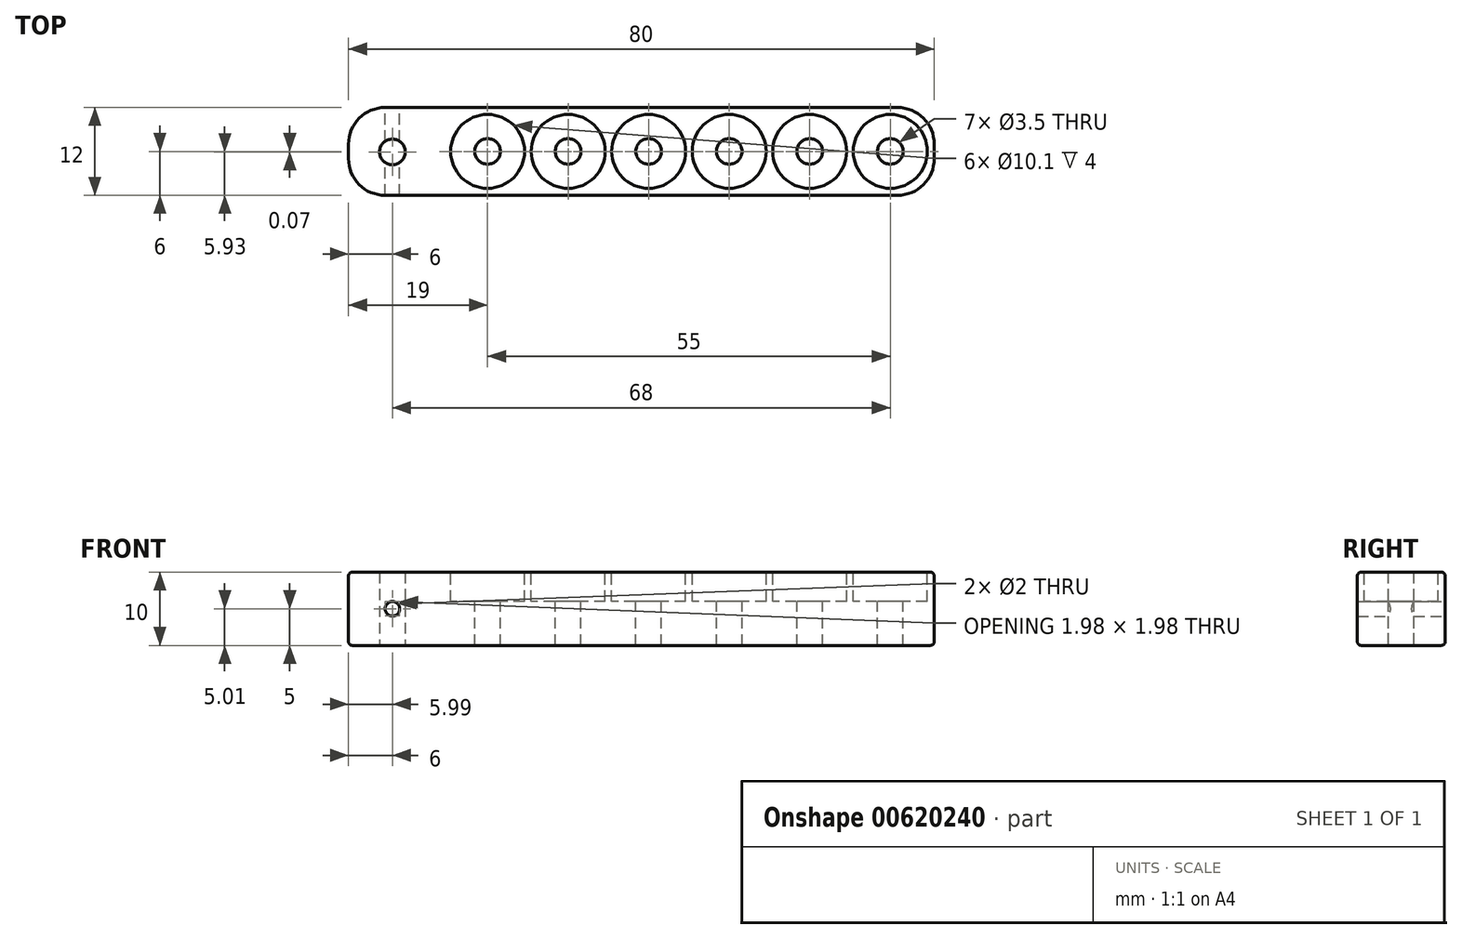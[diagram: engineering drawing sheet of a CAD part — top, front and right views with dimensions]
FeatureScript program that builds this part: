
annotation { "Feature Type Name" : "Feature", "Feature Type Description" : "" }
export const myFeature = defineFeature(function(context is Context, id is Id, definition is map)
    precondition{}
    {
        {
            var Q0;
            Q0=qCreatedBy(makeId("Top.planeOp"),FACE);
            var sketch = newSketch(context, id + "F0", { "sketchPlane" : qUnion([Q0])});
            skLineSegment(sketch, "E0.bottom", {"start": v(40, 6) * mm, "end": v(-40, 6) * mm});
            skLineSegment(sketch, "E0.top", {"start": v(40, -6) * mm, "end": v(-40, -6) * mm});
            skLineSegment(sketch, "E0.left", {"start": v(40, 6) * mm, "end": v(40, -6) * mm});
            skLineSegment(sketch, "E0.right", {"start": v(-40, 6) * mm, "end": v(-40, -6) * mm});
            skPoint(sketch, "E0.middle", {"position": v(0, 0) * mm});
            skSolve(sketch);
        }
        {
            var Q0;
            Q0=makeQuery(id+"F0.imprint","IMPRINT",FACE,{"disambiguationData":[TD([[makeQuery(id+"F0.imprint","IMPRINT",EDGE,{"derivedFrom":sQuery(id+"F0.wireOp",EDGE,"E0.bottom")}),1.0]])]});
            extrude(context, id + "F1", {"entities" : qUnion([Q0]), "depth" : 10 * mm, "offsetDistance" : 25 * mm});
        }
        {
            var Q0;
            Q0=makeQuery(id+"F1.opExtrude","CAP_FACE",FACE,{"disambiguationData":[OSD([sQuery(id+"F0.wireOp",EDGE,"E0.bottom"),sQuery(id+"F0.wireOp",EDGE,"E0.top"),sQuery(id+"F0.wireOp",EDGE,"E0.left"),sQuery(id+"F0.wireOp",EDGE,"E0.right")])],"isStart":false});
            var sketch = newSketch(context, id + "F2", { "sketchPlane" : qUnion([Q0])});
            skLineSegment(sketch, "E1", {"start": v(40, 0) * mm, "end": v(-40, 0) * mm, "construction": true});
            skCircle(sketch, "E2", {"center": v(34, 0) * mm, "radius": 5.05 * mm});
            skCircle(sketch, "E3", {"center": v(23, 0) * mm, "radius": 5.05 * mm});
            skCircle(sketch, "E4", {"center": v(12, 0) * mm, "radius": 5.05 * mm});
            skCircle(sketch, "E5", {"center": v(1, 0) * mm, "radius": 5.05 * mm});
            skCircle(sketch, "E6", {"center": v(-10, 0) * mm, "radius": 5.05 * mm});
            skCircle(sketch, "E7", {"center": v(-21, 0) * mm, "radius": 5.05 * mm});
            skSolve(sketch);
        }
        {
            var Q0;
            Q0 = qSketchRegion(id + "F2", true);
            extrude(context, id + "F3", {"entities" : qUnion([Q0]), "operationType" : NewBodyOperationType.REMOVE, "oppositeDirection" : true, "depth" : 4 * mm, "offsetDistance" : 25 * mm});
        }
        {
            var Q0;
            Q0=makeQuery(id+"F1.opExtrude","SWEPT_EDGE",EDGE,{"disambiguationData":[OSD([sQuery(id+"F0.wireOp",EDGE,"E0.top"),sQuery(id+"F0.wireOp",EDGE,"E0.left")])]});
            fillet(context, id + "F4", {"entities" : qUnion([Q0]), "radius" : 5 * mm, "tangentPropagation" : true, "allowEdgeOverflow" : false});
        }
        {
            var Q0;
            Q0=makeQuery(id+"F1.opExtrude","SWEPT_EDGE",EDGE,{"disambiguationData":[OSD([sQuery(id+"F0.wireOp",EDGE,"E0.bottom"),sQuery(id+"F0.wireOp",EDGE,"E0.left")])]});
            var Q1;
            Q1=makeQuery(id+"F1.opExtrude","SWEPT_EDGE",EDGE,{"disambiguationData":[OSD([sQuery(id+"F0.wireOp",EDGE,"E0.top"),sQuery(id+"F0.wireOp",EDGE,"E0.right")])]});
            var Q2;
            Q2=makeQuery(id+"F1.opExtrude","SWEPT_EDGE",EDGE,{"disambiguationData":[OSD([sQuery(id+"F0.wireOp",EDGE,"E0.bottom"),sQuery(id+"F0.wireOp",EDGE,"E0.right")])]});
            fillet(context, id + "F5", {"entities" : qUnion([Q0, Q1, Q2]), "radius" : 5 * mm, "tangentPropagation" : true, "allowEdgeOverflow" : false});
        }
        {
            var Q0;
            Q0=makeQuery(id+"F3.boolean.opBoolean","COPY",FACE,{"derivedFrom":makeQuery(id+"F3.opExtrude","CAP_FACE",FACE,{"disambiguationData":[OSD([sQuery(id+"F2.wireOp",EDGE,"E7")])],"isStart":false})});
            var sketch = newSketch(context, id + "F6", { "sketchPlane" : qUnion([Q0])});
            skLineSegment(sketch, "E8", {"start": v(-39.92, 0) * mm, "end": v(40.18, 0) * mm, "construction": true});
            skCircle(sketch, "E9", {"center": v(34, 0) * mm, "radius": 1.75 * mm});
            skCircle(sketch, "E10", {"center": v(23, 0) * mm, "radius": 1.75 * mm});
            skCircle(sketch, "E11", {"center": v(12, 0) * mm, "radius": 1.75 * mm});
            skCircle(sketch, "E12", {"center": v(1, 0) * mm, "radius": 1.75 * mm});
            skCircle(sketch, "E13", {"center": v(-10, 0) * mm, "radius": 1.75 * mm});
            skCircle(sketch, "E14", {"center": v(-21, 0) * mm, "radius": 1.75 * mm});
            skSolve(sketch);
        }
        {
            var Q0;
            Q0 = qSketchRegion(id + "F6", true);
            extrude(context, id + "F7", {"entities" : qUnion([Q0]), "operationType" : NewBodyOperationType.REMOVE, "oppositeDirection" : true, "depth" : 25 * mm, "offsetDistance" : 25 * mm});
        }
        {
            var Q0;
            Q0=makeQuery(id+"F1.opExtrude","CAP_EDGE",EDGE,{"disambiguationData":[OSD([sQuery(id+"F0.wireOp",EDGE,"E0.top")])],"isStart":false});
            var Q1;
            {var subQ0=sQuery(id+"F0.wireOp",EDGE,"E0.left");var subQ1=sQuery(id+"F0.wireOp",EDGE,"E0.top");Q1=makeQuery(id+"F4.opFillet","BLEND_EDGE",EDGE,{"blendedFrom":[makeQuery(id+"F1.opExtrude","SWEPT_EDGE",EDGE,{"disambiguationData":[OSD([subQ1,subQ0])]}),makeQuery(id+"F1.opExtrude","CAP_FACE",FACE,{"disambiguationData":[OSD([sQuery(id+"F0.wireOp",EDGE,"E0.bottom"),subQ1,subQ0,sQuery(id+"F0.wireOp",EDGE,"E0.right")])],"isStart":false})],"blendedInto":[makeQuery(id+"F1.opExtrude","CAP_FACE",FACE,{"disambiguationData":[OSD([sQuery(id+"F0.wireOp",EDGE,"E0.bottom"),subQ1,subQ0,sQuery(id+"F0.wireOp",EDGE,"E0.right")])],"isStart":false})]});}
            var Q2;
            {var subQ0=sQuery(id+"F0.wireOp",EDGE,"E0.left");var subQ1=sQuery(id+"F0.wireOp",EDGE,"E0.bottom");Q2=makeQuery(id+"F5.opFillet","BLEND_EDGE",EDGE,{"blendedFrom":[makeQuery(id+"F1.opExtrude","SWEPT_EDGE",EDGE,{"disambiguationData":[OSD([subQ1,subQ0])]}),makeQuery(id+"F1.opExtrude","CAP_FACE",FACE,{"disambiguationData":[OSD([subQ1,sQuery(id+"F0.wireOp",EDGE,"E0.top"),subQ0,sQuery(id+"F0.wireOp",EDGE,"E0.right")])],"isStart":false})],"blendedInto":[makeQuery(id+"F1.opExtrude","CAP_FACE",FACE,{"disambiguationData":[OSD([subQ1,sQuery(id+"F0.wireOp",EDGE,"E0.top"),subQ0,sQuery(id+"F0.wireOp",EDGE,"E0.right")])],"isStart":false})]});}
            var Q3;
            Q3=makeQuery(id+"F1.opExtrude","CAP_EDGE",EDGE,{"disambiguationData":[OSD([sQuery(id+"F0.wireOp",EDGE,"E0.bottom")])],"isStart":false});
            var Q4;
            {var subQ0=sQuery(id+"F0.wireOp",EDGE,"E0.right");var subQ1=sQuery(id+"F0.wireOp",EDGE,"E0.top");Q4=makeQuery(id+"F5.opFillet","BLEND_EDGE",EDGE,{"blendedFrom":[makeQuery(id+"F1.opExtrude","SWEPT_EDGE",EDGE,{"disambiguationData":[OSD([subQ1,subQ0])]}),makeQuery(id+"F1.opExtrude","CAP_FACE",FACE,{"disambiguationData":[OSD([sQuery(id+"F0.wireOp",EDGE,"E0.bottom"),subQ1,sQuery(id+"F0.wireOp",EDGE,"E0.left"),subQ0])],"isStart":false})],"blendedInto":[makeQuery(id+"F1.opExtrude","CAP_FACE",FACE,{"disambiguationData":[OSD([sQuery(id+"F0.wireOp",EDGE,"E0.bottom"),subQ1,sQuery(id+"F0.wireOp",EDGE,"E0.left"),subQ0])],"isStart":false})]});}
            fillet(context, id + "F8", {"entities" : qUnion([Q0, Q1, Q2, Q3, Q4]), "radius" : 0.5 * mm, "tangentPropagation" : true, "allowEdgeOverflow" : false});
        }
        {
            var Q0;
            Q0=makeQuery(id+"F1.opExtrude","CAP_EDGE",EDGE,{"disambiguationData":[OSD([sQuery(id+"F0.wireOp",EDGE,"E0.top")])],"isStart":true});
            var Q1;
            {var subQ0=sQuery(id+"F0.wireOp",EDGE,"E0.right");var subQ1=sQuery(id+"F0.wireOp",EDGE,"E0.top");Q1=makeQuery(id+"F5.opFillet","BLEND_EDGE",EDGE,{"blendedFrom":[makeQuery(id+"F1.opExtrude","SWEPT_EDGE",EDGE,{"disambiguationData":[OSD([subQ1,subQ0])]}),makeQuery(id+"F1.opExtrude","CAP_FACE",FACE,{"disambiguationData":[OSD([sQuery(id+"F0.wireOp",EDGE,"E0.bottom"),subQ1,sQuery(id+"F0.wireOp",EDGE,"E0.left"),subQ0])],"isStart":true})],"blendedInto":[makeQuery(id+"F1.opExtrude","CAP_FACE",FACE,{"disambiguationData":[OSD([sQuery(id+"F0.wireOp",EDGE,"E0.bottom"),subQ1,sQuery(id+"F0.wireOp",EDGE,"E0.left"),subQ0])],"isStart":true})]});}
            var Q2;
            Q2=makeQuery(id+"F1.opExtrude","CAP_EDGE",EDGE,{"disambiguationData":[OSD([sQuery(id+"F0.wireOp",EDGE,"E0.bottom")])],"isStart":true});
            var Q3;
            {var subQ0=sQuery(id+"F0.wireOp",EDGE,"E0.left");var subQ1=sQuery(id+"F0.wireOp",EDGE,"E0.bottom");Q3=makeQuery(id+"F5.opFillet","BLEND_EDGE",EDGE,{"blendedFrom":[makeQuery(id+"F1.opExtrude","SWEPT_EDGE",EDGE,{"disambiguationData":[OSD([subQ1,subQ0])]}),makeQuery(id+"F1.opExtrude","CAP_FACE",FACE,{"disambiguationData":[OSD([subQ1,sQuery(id+"F0.wireOp",EDGE,"E0.top"),subQ0,sQuery(id+"F0.wireOp",EDGE,"E0.right")])],"isStart":true})],"blendedInto":[makeQuery(id+"F1.opExtrude","CAP_FACE",FACE,{"disambiguationData":[OSD([subQ1,sQuery(id+"F0.wireOp",EDGE,"E0.top"),subQ0,sQuery(id+"F0.wireOp",EDGE,"E0.right")])],"isStart":true})]});}
            var Q4;
            {var subQ0=sQuery(id+"F0.wireOp",EDGE,"E0.left");var subQ1=sQuery(id+"F0.wireOp",EDGE,"E0.top");Q4=makeQuery(id+"F4.opFillet","BLEND_EDGE",EDGE,{"blendedFrom":[makeQuery(id+"F1.opExtrude","SWEPT_EDGE",EDGE,{"disambiguationData":[OSD([subQ1,subQ0])]}),makeQuery(id+"F1.opExtrude","CAP_FACE",FACE,{"disambiguationData":[OSD([sQuery(id+"F0.wireOp",EDGE,"E0.bottom"),subQ1,subQ0,sQuery(id+"F0.wireOp",EDGE,"E0.right")])],"isStart":true})],"blendedInto":[makeQuery(id+"F1.opExtrude","CAP_FACE",FACE,{"disambiguationData":[OSD([sQuery(id+"F0.wireOp",EDGE,"E0.bottom"),subQ1,subQ0,sQuery(id+"F0.wireOp",EDGE,"E0.right")])],"isStart":true})]});}
            fillet(context, id + "F9", {"entities" : qUnion([Q0, Q1, Q2, Q3, Q4]), "radius" : 0.5 * mm, "tangentPropagation" : true, "allowEdgeOverflow" : false});
        }
        {
            var Q0;
            Q0=makeQuery(id+"F1.opExtrude","CAP_FACE",FACE,{"disambiguationData":[OSD([sQuery(id+"F0.wireOp",EDGE,"E0.bottom"),sQuery(id+"F0.wireOp",EDGE,"E0.top"),sQuery(id+"F0.wireOp",EDGE,"E0.left"),sQuery(id+"F0.wireOp",EDGE,"E0.right")])],"isStart":true});
            var sketch = newSketch(context, id + "F10", { "sketchPlane" : qUnion([Q0])});
            skLineSegment(sketch, "E15", {"start": v(39.5, 1) * mm, "end": v(-39.5, 0) * mm, "construction": true});
            skCircle(sketch, "E16", {"center": v(-34, 0.07) * mm, "radius": 1.75 * mm});
            skSolve(sketch);
        }
        {
            var Q0;
            Q0 = qSketchRegion(id + "F10", true);
            extrude(context, id + "F11", {"entities" : qUnion([Q0]), "operationType" : NewBodyOperationType.REMOVE, "oppositeDirection" : true, "depth" : 25 * mm, "offsetDistance" : 25 * mm});
        }
        {
            var Q0;
            Q0=makeQuery(id+"F1.opExtrude","SWEPT_FACE",FACE,{"disambiguationData":[OSD([sQuery(id+"F0.wireOp",EDGE,"E0.bottom")])]});
            var sketch = newSketch(context, id + "F12", { "sketchPlane" : qUnion([Q0])});
            skLineSegment(sketch, "E17", {"start": v(-35, 5) * mm, "end": v(35, 5) * mm, "construction": true});
            skCircle(sketch, "E18", {"center": v(34, 5) * mm, "radius": 1 * mm});
            skSolve(sketch);
        }
        {
            var Q0;
            Q0 = qSketchRegion(id + "F12", true);
            extrude(context, id + "F13", {"entities" : qUnion([Q0]), "operationType" : NewBodyOperationType.REMOVE, "oppositeDirection" : true, "depth" : 25 * mm, "offsetDistance" : 25 * mm});
        }
    });
